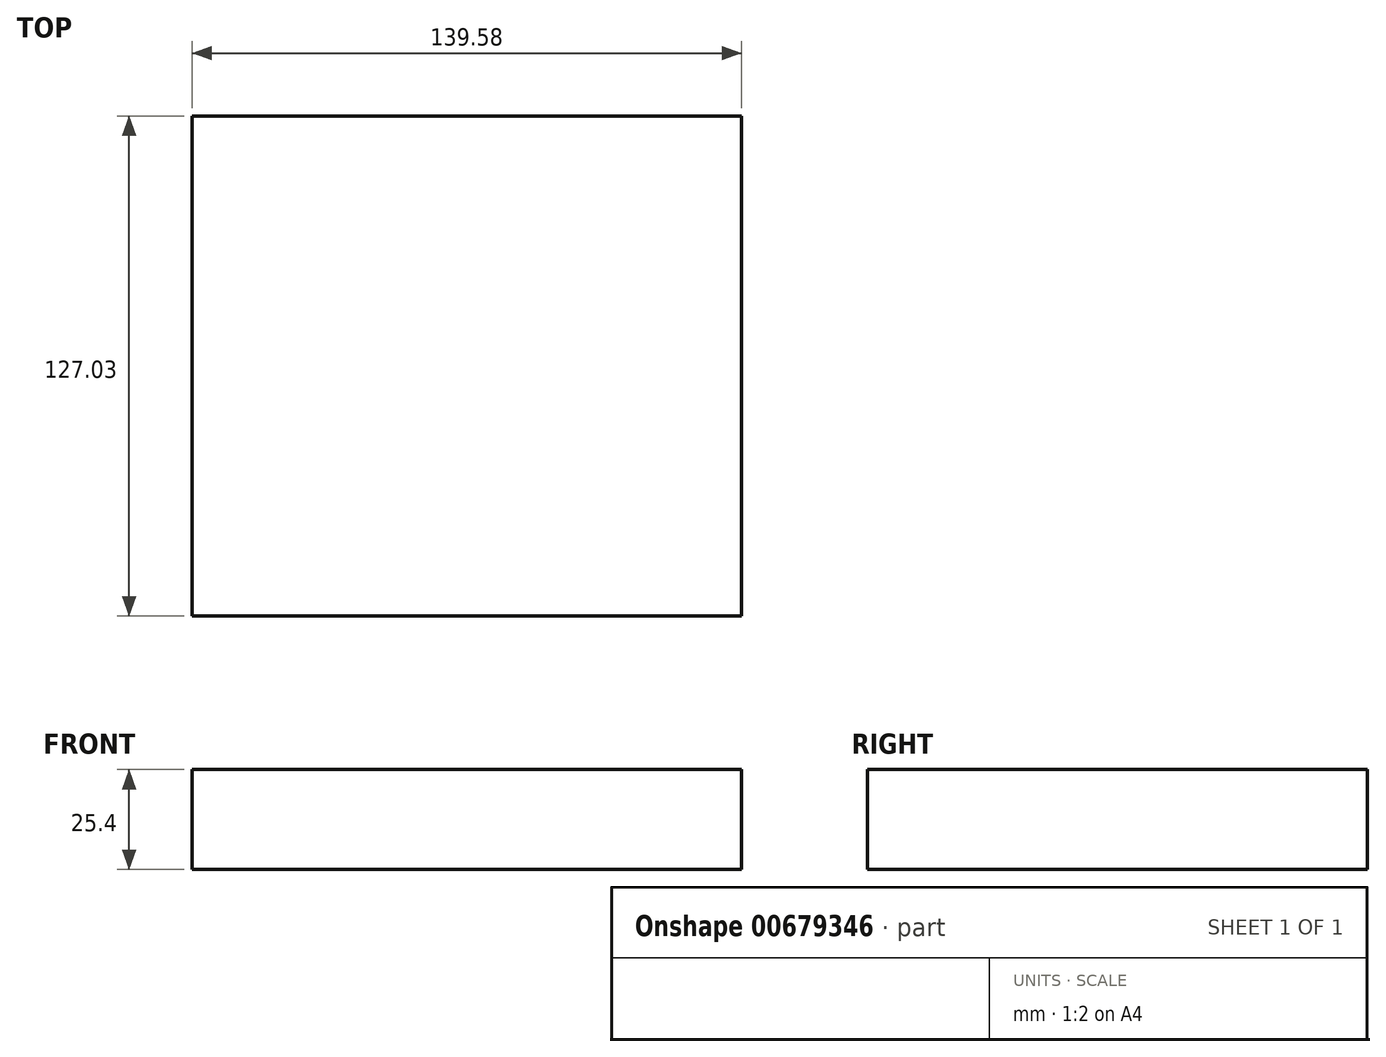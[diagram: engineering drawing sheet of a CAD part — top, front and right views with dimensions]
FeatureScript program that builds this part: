
annotation { "Feature Type Name" : "Feature", "Feature Type Description" : "" }
export const myFeature = defineFeature(function(context is Context, id is Id, definition is map)
    precondition{}
    {
        {
            var Q0;
            Q0=qCreatedBy(makeId("Top.planeOp"),FACE);
            var sketch = newSketch(context, id + "F0", { "sketchPlane" : qUnion([Q0])});
            skLineSegment(sketch, "E0.bottom", {"start": v(-71.4, 58.26) * mm, "end": v(68.18, 58.26) * mm});
            skLineSegment(sketch, "E0.top", {"start": v(-71.4, -68.77) * mm, "end": v(68.18, -68.77) * mm});
            skLineSegment(sketch, "E0.left", {"start": v(-71.4, 58.26) * mm, "end": v(-71.4, -68.77) * mm});
            skLineSegment(sketch, "E0.right", {"start": v(68.18, 58.26) * mm, "end": v(68.18, -68.77) * mm});
            skLineSegment(sketch, "E1", {"start": v(-71.4, 0) * mm, "end": v(68.18, 0) * mm});
            skLineSegment(sketch, "E2", {"start": v(0, -68.77) * mm, "end": v(0, 58.26) * mm});
            skLineSegment(sketch, "E3", {"start": v(-71.4, 28.47) * mm, "end": v(68.18, 28.47) * mm});
            skPoint(sketch, "E3.endSnap0", {"position": v(68.18, -5.26) * mm});
            skLineSegment(sketch, "E4", {"start": v(-71.4, -33.73) * mm, "end": v(68.18, -33.73) * mm});
            skSolve(sketch);
        }
        {
            var Q0;
            {var subQ0=sQuery(id+"F0.wireOp",EDGE,"E0.left");var subQ1=sQuery(id+"F0.wireOp",EDGE,"E0.bottom");var subQ2=makeQuery(id+"F0.imprint","INTERSECT",VERTEX,{"derivedFrom":[subQ1,subQ0]});Q0=makeQuery(id+"F0.imprint","IMPRINT",FACE,{"disambiguationData":[TD([[makeQuery(id+"F0.imprint","IMPRINT",EDGE,{"disambiguationData":[TD([[subQ2,-1.0]])],"derivedFrom":subQ1}),-1.0]])]});}
            var Q1;
            {var subQ0=sQuery(id+"F0.wireOp",EDGE,"E0.right");var subQ1=sQuery(id+"F0.wireOp",EDGE,"E0.bottom");var subQ2=makeQuery(id+"F0.imprint","INTERSECT",VERTEX,{"derivedFrom":[subQ1,subQ0]});Q1=makeQuery(id+"F0.imprint","IMPRINT",FACE,{"disambiguationData":[TD([[makeQuery(id+"F0.imprint","IMPRINT",EDGE,{"disambiguationData":[TD([[subQ2,1.0]])],"derivedFrom":subQ1}),-1.0]])]});}
            var Q2;
            {var subQ0=sQuery(id+"F0.wireOp",EDGE,"E0.left");var subQ1=sQuery(id+"F0.wireOp",EDGE,"E0.top");var subQ2=makeQuery(id+"F0.imprint","INTERSECT",VERTEX,{"derivedFrom":[subQ1,subQ0]});Q2=makeQuery(id+"F0.imprint","IMPRINT",FACE,{"disambiguationData":[TD([[makeQuery(id+"F0.imprint","IMPRINT",EDGE,{"disambiguationData":[TD([[subQ2,-1.0]])],"derivedFrom":subQ1}),1.0]])]});}
            var Q3;
            {var subQ0=sQuery(id+"F0.wireOp",EDGE,"E0.right");var subQ1=sQuery(id+"F0.wireOp",EDGE,"E0.top");var subQ2=makeQuery(id+"F0.imprint","INTERSECT",VERTEX,{"derivedFrom":[subQ1,subQ0]});Q3=makeQuery(id+"F0.imprint","IMPRINT",FACE,{"disambiguationData":[TD([[makeQuery(id+"F0.imprint","IMPRINT",EDGE,{"disambiguationData":[TD([[subQ2,1.0]])],"derivedFrom":subQ1}),1.0]])]});}
            var Q4;
            {var subQ0=sQuery(id+"F0.wireOp",EDGE,"E1");var subQ1=sQuery(id+"F0.wireOp",EDGE,"E0.left");var subQ2=makeQuery(id+"F0.imprint","INTERSECT",VERTEX,{"derivedFrom":[subQ1,subQ0]});Q4=makeQuery(id+"F0.imprint","IMPRINT",FACE,{"disambiguationData":[TD([[makeQuery(id+"F0.imprint","IMPRINT",EDGE,{"disambiguationData":[TD([[subQ2,-1.0]])],"derivedFrom":subQ1}),1.0]])]});}
            var Q5;
            {var subQ0=sQuery(id+"F0.wireOp",EDGE,"E1");var subQ1=sQuery(id+"F0.wireOp",EDGE,"E0.right");var subQ2=makeQuery(id+"F0.imprint","INTERSECT",VERTEX,{"derivedFrom":[subQ1,subQ0]});Q5=makeQuery(id+"F0.imprint","IMPRINT",FACE,{"disambiguationData":[TD([[makeQuery(id+"F0.imprint","IMPRINT",EDGE,{"disambiguationData":[TD([[subQ2,1.0]])],"derivedFrom":subQ1}),-1.0]])]});}
            var Q6;
            {var subQ0=sQuery(id+"F0.wireOp",EDGE,"E1");var subQ1=sQuery(id+"F0.wireOp",EDGE,"E0.right");var subQ2=makeQuery(id+"F0.imprint","INTERSECT",VERTEX,{"derivedFrom":[subQ1,subQ0]});Q6=makeQuery(id+"F0.imprint","IMPRINT",FACE,{"disambiguationData":[TD([[makeQuery(id+"F0.imprint","IMPRINT",EDGE,{"disambiguationData":[TD([[subQ2,-1.0]])],"derivedFrom":subQ1}),-1.0]])]});}
            var Q7;
            {var subQ0=sQuery(id+"F0.wireOp",EDGE,"E1");var subQ1=sQuery(id+"F0.wireOp",EDGE,"E0.left");var subQ2=makeQuery(id+"F0.imprint","INTERSECT",VERTEX,{"derivedFrom":[subQ1,subQ0]});Q7=makeQuery(id+"F0.imprint","IMPRINT",FACE,{"disambiguationData":[TD([[makeQuery(id+"F0.imprint","IMPRINT",EDGE,{"disambiguationData":[TD([[subQ2,1.0]])],"derivedFrom":subQ1}),1.0]])]});}
            extrude(context, id + "F1", {"entities" : qUnion([Q0, Q1, Q2, Q3, Q4, Q5, Q6, Q7]), "depth" : 25.4 * mm, "offsetDistance" : 25.4 * mm});
        }
    });
